# Revit family: Sileo
name_source: partatom
category: Mechanical Equipment
units: mm (PartAtom-declared; Revit-internal decimal feet)

## family parameters
Always vertical = Yes
Classification = None
Cut with Voids When Loaded = No
Part Type = Normal
Room Calculation Point = No
Round Connector Dimension = Use Diameter
Shared = No
Work Plane-Based = No

## types (4) — shared parameters
00_20_Manufacturer = Blauberg
00_20_Name = Axial fan
Amperage = 0 A
Casing Material = Plastic, opaque, white
Description = For round channels
Frequency = 50 Hz
Load Classification = HVAC
Maintenance zone material = <By Category>
Manufacturer = Blauberg
Number of Fase = 1
URL = https://blaubergventilatoren.de
Voltage = 230 V
zero-valued in all types: Default Elevation

## per-type parameters (varying)
| type | Apparent Load | Diameter | Dy | H | Height | Length | Maximum Air Flow | Power | Sound pressure level at 3 m distance | Weight | Width | b | c | d | e |
| Sileo 100 | 12 W | 100 mm  [stored 0.328084 ft] | 96 mm  [stored 0.314961 ft] | 158 mm | 158 mm | 107 mm  [stored 0.35105 ft] | 97.0 m³/h | 8 W | 25 dBA | 0.55 kg | 158 mm | 158 mm | 81 mm  [stored 0.265748 ft] | 100 mm  [stored 0.328084 ft] | 26 mm |
| Sileo 125 | 25 W | 124 mm  [stored 0.406824 ft] | 120 mm  [stored 0.393701 ft] | 182 mm  [stored 0.597113 ft] | 182 mm  [stored 0.597113 ft] | 118 mm | 187.0 m³/h | 17 W | 32 dBA | 0.78 kg | 182 mm  [stored 0.597113 ft] | 182 mm  [stored 0.597113 ft] | 91 mm  [stored 0.298556 ft] | 124 mm  [stored 0.406824 ft] | 27 mm  [stored 0.0885827 ft] |
| Sileo 150 | 21 W | 148 mm  [stored 0.485564 ft] | 144 mm  [stored 0.472441 ft] | 214 mm  [stored 0.7021 ft] | 214 mm  [stored 0.7021 ft] | 130 mm  [stored 0.426509 ft] | 315.0 m³/h | 19 W | 33 dBA | 1.33 kg | 214 mm  [stored 0.7021 ft] | 214 mm  [stored 0.7021 ft] | 98 mm  [stored 0.321522 ft] | 148 mm  [stored 0.485564 ft] | 32 mm  [stored 0.104987 ft] |
| Sileo Max 150 | 23 W | 150 mm | 146 mm  [stored 0.479003 ft] | 214 mm  [stored 0.7021 ft] | 214 mm  [stored 0.7021 ft] | 130 mm  [stored 0.426509 ft] | 370.0 m³/h | 22 W | 38 dBA | 1.33 kg | 214 mm  [stored 0.7021 ft] | 214 mm  [stored 0.7021 ft] | 98 mm  [stored 0.321522 ft] | 150 mm | 32 mm  [stored 0.104987 ft] |

note: column(s) folded — value = type name in every type: 00_20_Type

note: [stored X ft] marks values corroborated as IEEE doubles in the binary element streams (Revit-internal decimal feet)
